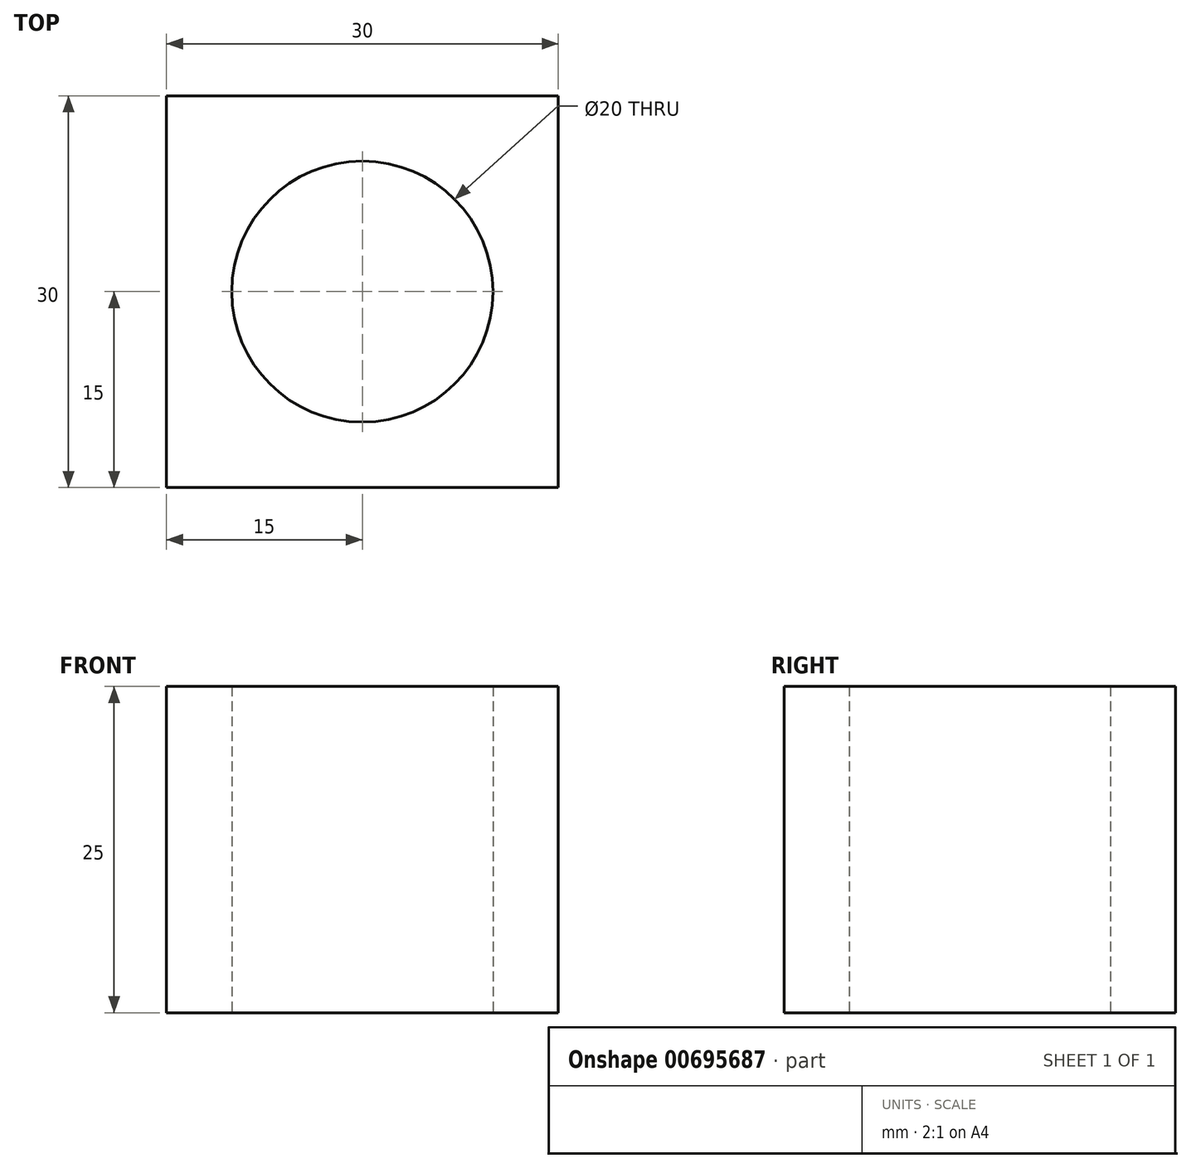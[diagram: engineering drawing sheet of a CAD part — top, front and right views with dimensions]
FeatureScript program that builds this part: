
annotation { "Feature Type Name" : "Feature", "Feature Type Description" : "" }
export const myFeature = defineFeature(function(context is Context, id is Id, definition is map)
    precondition{}
    {
        {
            var Q0;
            Q0=qCreatedBy(makeId("Top.planeOp"),FACE);
            var sketch = newSketch(context, id + "F0", { "sketchPlane" : qUnion([Q0])});
            skLineSegment(sketch, "E0.bottom", {"start": v(15, 15) * mm, "end": v(-15, 15) * mm});
            skLineSegment(sketch, "E0.top", {"start": v(15, -15) * mm, "end": v(-15, -15) * mm});
            skLineSegment(sketch, "E0.left", {"start": v(15, 15) * mm, "end": v(15, -15) * mm});
            skLineSegment(sketch, "E0.right", {"start": v(-15, 15) * mm, "end": v(-15, -15) * mm});
            skPoint(sketch, "E0.middle", {"position": v(0, 0) * mm});
            skCircle(sketch, "E1", {"center": v(0, 0) * mm, "radius": 10 * mm});
            skSolve(sketch);
        }
        {
            var Q0;
            Q0 = qSketchRegion(id + "F0", true);
            extrude(context, id + "F1", {"entities" : qUnion([Q0]), "depth" : 25 * mm, "offsetDistance" : 25 * mm});
        }
    });
